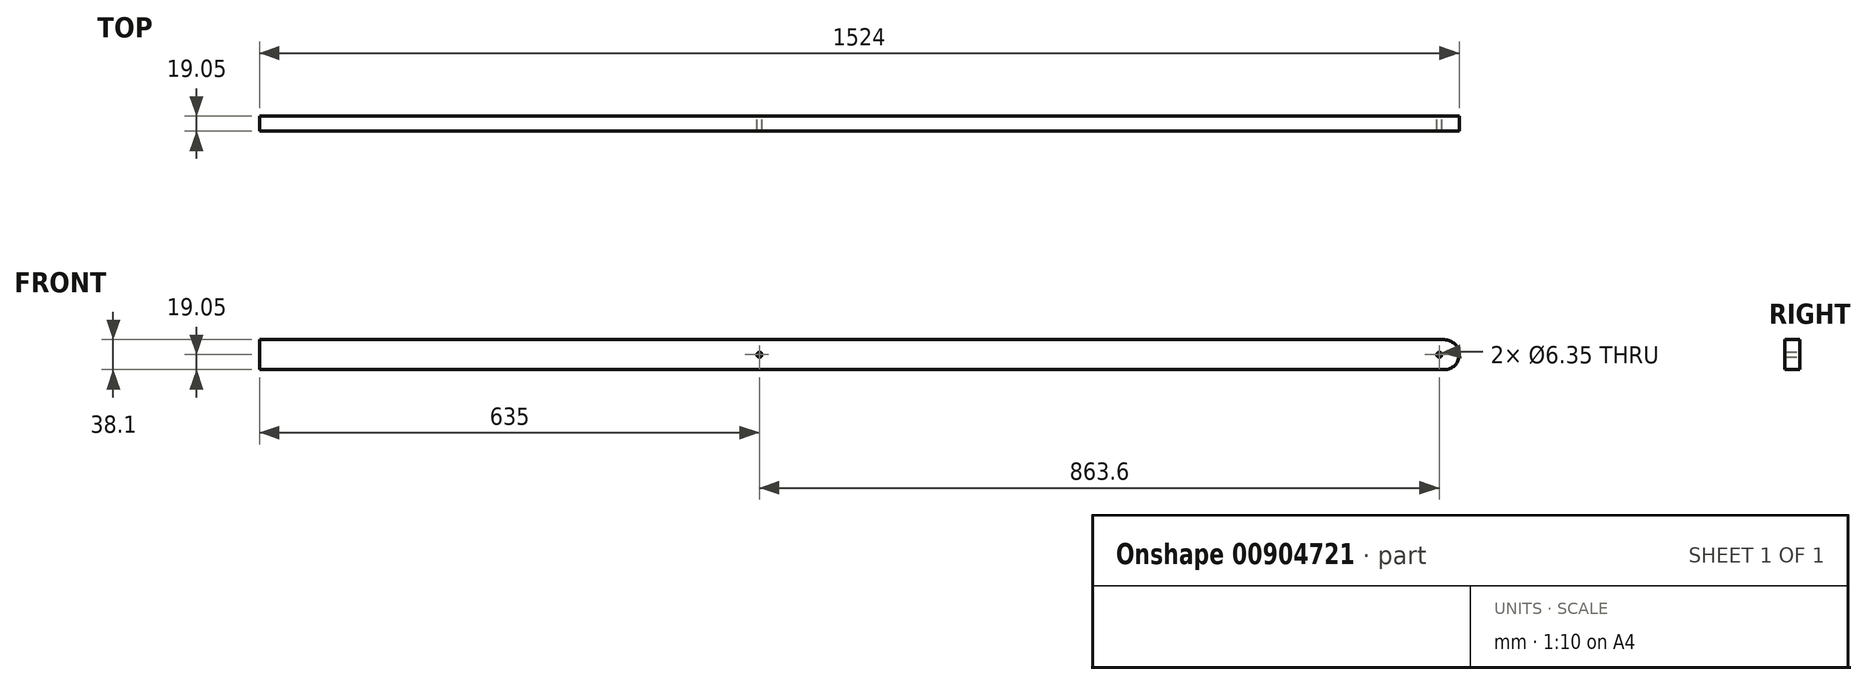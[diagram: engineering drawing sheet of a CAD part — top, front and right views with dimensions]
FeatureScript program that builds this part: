
annotation { "Feature Type Name" : "Feature", "Feature Type Description" : "" }
export const myFeature = defineFeature(function(context is Context, id is Id, definition is map)
    precondition{}
    {
        {
            var Q0;
            Q0=qCreatedBy(makeId("Front.planeOp"),FACE);
            var sketch = newSketch(context, id + "F0", { "sketchPlane" : qUnion([Q0])});
            skLineSegment(sketch, "E0.bottom", {"start": v(-762, -19.05) * mm, "end": v(762, -19.05) * mm});
            skLineSegment(sketch, "E0.top", {"start": v(-762, 19.05) * mm, "end": v(762, 19.05) * mm});
            skLineSegment(sketch, "E0.left", {"start": v(-762, -19.05) * mm, "end": v(-762, 19.05) * mm});
            skLineSegment(sketch, "E0.right", {"start": v(762, -19.05) * mm, "end": v(762, 19.05) * mm});
            skPoint(sketch, "E0.middle", {"position": v(0, 0) * mm});
            skPoint(sketch, "E1", {"position": v(736.6, 0) * mm});
            skCircle(sketch, "E2", {"center": v(736.6, 0) * mm, "radius": 3.18 * mm});
            skCircle(sketch, "E3", {"center": v(-127, 0) * mm, "radius": 3.18 * mm});
            skSolve(sketch);
        }
        {
            var Q0;
            Q0 = qSketchRegion(id + "F0", true);
            extrude(context, id + "F1", {"entities" : qUnion([Q0]), "depth" : 19.05 * mm, "offsetDistance" : 25.4 * mm});
        }
        {
            var Q0;
            Q0=makeQuery(id+"F1.opExtrude","SWEPT_EDGE",EDGE,{"disambiguationData":[OSD([sQuery(id+"F0.wireOp",EDGE,"E0.top"),sQuery(id+"F0.wireOp",EDGE,"E0.right")])]});
            var Q1;
            Q1=makeQuery(id+"F1.opExtrude","SWEPT_EDGE",EDGE,{"disambiguationData":[OSD([sQuery(id+"F0.wireOp",EDGE,"E0.bottom"),sQuery(id+"F0.wireOp",EDGE,"E0.right")])]});
            fillet(context, id + "F2", {"entities" : qUnion([Q0, Q1]), "radius" : 19.05 * mm, "tangentPropagation" : true, "allowEdgeOverflow" : false});
        }
    });
